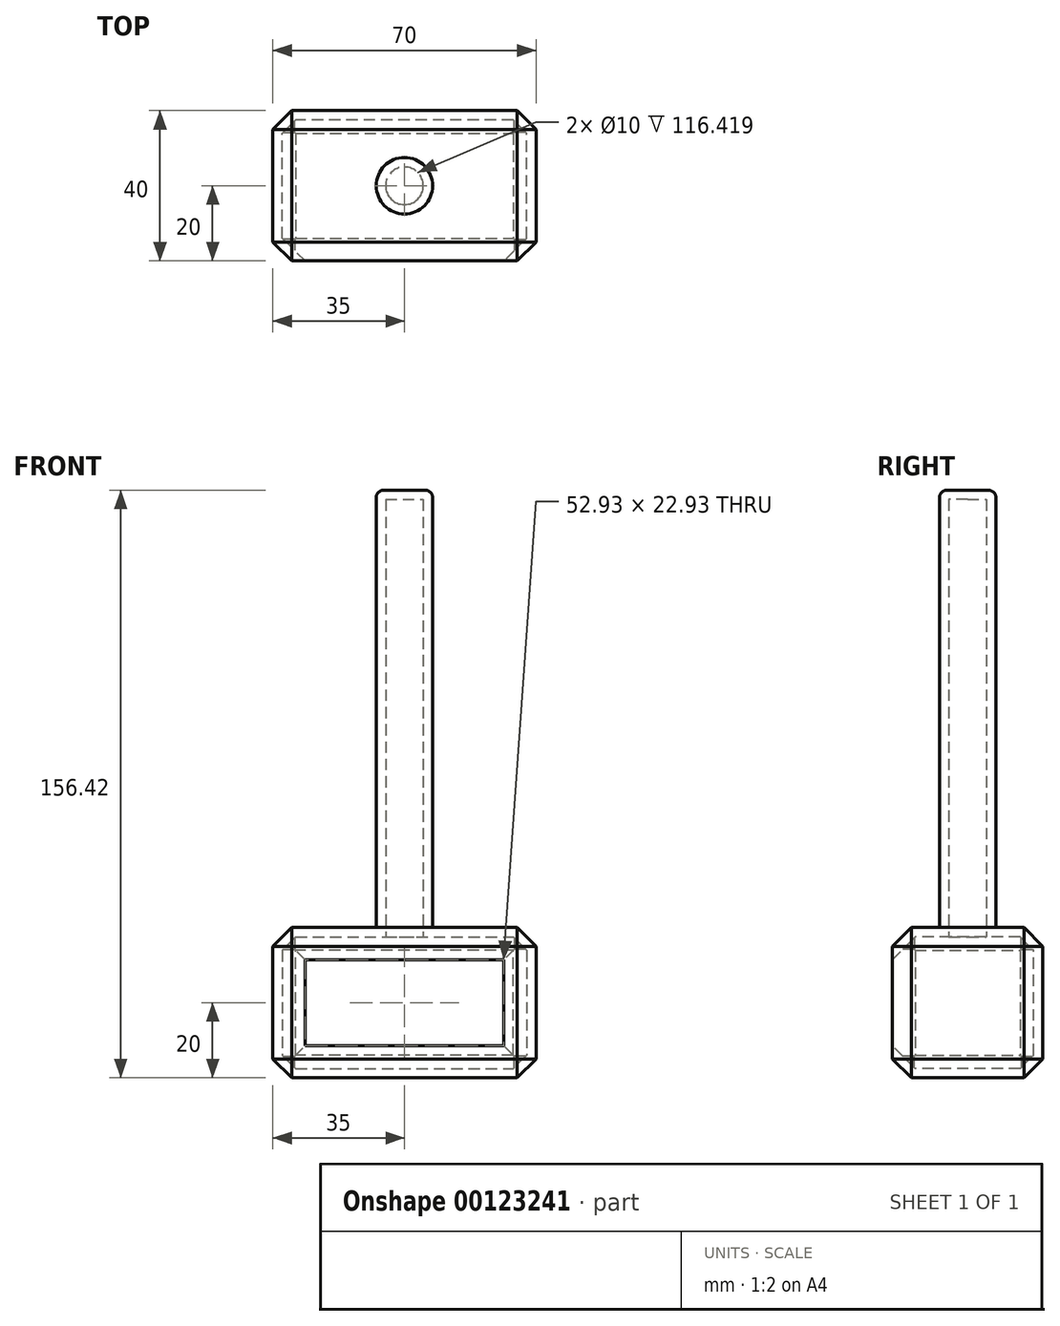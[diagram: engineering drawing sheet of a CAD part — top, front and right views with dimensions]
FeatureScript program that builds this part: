
annotation { "Feature Type Name" : "Feature", "Feature Type Description" : "" }
export const myFeature = defineFeature(function(context is Context, id is Id, definition is map)
    precondition{}
    {
        {
            var Q0;
            Q0=qCreatedBy(makeId("Front.planeOp"),FACE);
            var sketch = newSketch(context, id + "F0", { "sketchPlane" : qUnion([Q0])});
            skLineSegment(sketch, "E0", {"start": v(0, 0) * mm, "end": v(-35, 0) * mm});
            skLineSegment(sketch, "E1", {"start": v(-35, 0) * mm, "end": v(-35, 40) * mm});
            skLineSegment(sketch, "E2", {"start": v(-35, 40) * mm, "end": v(0, 40) * mm});
            skLineSegment(sketch, "E3.MirrorCS", {"start": v(35, 40) * mm, "end": v(0, 40) * mm});
            skLineSegment(sketch, "E4.MirrorCS", {"start": v(35, 0) * mm, "end": v(35, 40) * mm});
            skLineSegment(sketch, "E5.MirrorCS", {"start": v(0, 0) * mm, "end": v(35, 0) * mm});
            skSolve(sketch);
        }
        {
            var Q0;
            Q0=makeQuery(id+"F0.imprint","IMPRINT",FACE,{"disambiguationData":[TD([[makeQuery(id+"F0.imprint","IMPRINT",EDGE,{"derivedFrom":sQuery(id+"F0.wireOp",EDGE,"E0")}),-1.0]])]});
            extrude(context, id + "F1", {"entities" : qUnion([Q0]), "depth" : 40 * mm});
        }
        {
            var Q0;
            Q0=makeQuery(id+"F1.opExtrude","SWEPT_FACE",FACE,{"disambiguationData":[OSD([sQuery(id+"F0.wireOp",EDGE,"E2"),sQuery(id+"F0.wireOp",EDGE,"E3.MirrorCS")])]});
            var sketch = newSketch(context, id + "F2", { "sketchPlane" : qUnion([Q0])});
            skLineSegment(sketch, "E6", {"start": v(0, 0) * mm, "end": v(0, -20) * mm});
            skCircle(sketch, "E7", {"center": v(0, -20) * mm, "radius": 7.5 * mm});
            skSolve(sketch);
        }
        {
            var Q0;
            Q0=makeQuery(id+"F2.imprint","IMPRINT",FACE,{"disambiguationData":[TD([[makeQuery(id+"F2.imprint","IMPRINT",EDGE,{"derivedFrom":sQuery(id+"F2.wireOp",EDGE,"E7")}),1.0]])]});
            var Q1;
            Q1=sQuery(id+"F2.wireOp",EDGE,"E7");
            extrude(context, id + "F3", {"entities" : qUnion([Q0]), "operationType" : NewBodyOperationType.ADD, "surfaceEntities" : qUnion([Q1]), "depth" : 116.42 * mm});
        }
        {
            var Q0;
            Q0=makeQuery(id+"F1.opExtrude","CAP_EDGE",EDGE,{"disambiguationData":[OSD([sQuery(id+"F0.wireOp",EDGE,"E2"),sQuery(id+"F0.wireOp",EDGE,"E3.MirrorCS")])],"isStart":false});
            var Q1;
            Q1=makeQuery(id+"F1.opExtrude","SWEPT_EDGE",EDGE,{"disambiguationData":[OSD([sQuery(id+"F0.wireOp",EDGE,"E1"),sQuery(id+"F0.wireOp",EDGE,"E2")])]});
            var Q2;
            Q2=makeQuery(id+"F1.opExtrude","CAP_EDGE",EDGE,{"disambiguationData":[OSD([sQuery(id+"F0.wireOp",EDGE,"E2"),sQuery(id+"F0.wireOp",EDGE,"E3.MirrorCS")])],"isStart":true});
            var Q3;
            Q3=makeQuery(id+"F1.opExtrude","SWEPT_EDGE",EDGE,{"disambiguationData":[OSD([sQuery(id+"F0.wireOp",EDGE,"E3.MirrorCS"),sQuery(id+"F0.wireOp",EDGE,"E4.MirrorCS")])]});
            var Q4;
            Q4=makeQuery(id+"F1.opExtrude","CAP_EDGE",EDGE,{"disambiguationData":[OSD([sQuery(id+"F0.wireOp",EDGE,"E4.MirrorCS")])],"isStart":false});
            var Q5;
            Q5=makeQuery(id+"F1.opExtrude","CAP_EDGE",EDGE,{"disambiguationData":[OSD([sQuery(id+"F0.wireOp",EDGE,"E1")])],"isStart":false});
            var Q6;
            Q6=makeQuery(id+"F1.opExtrude","SWEPT_FACE",FACE,{"disambiguationData":[OSD([sQuery(id+"F0.wireOp",EDGE,"E4.MirrorCS")])]});
            var Q7;
            Q7=makeQuery(id+"F1.opExtrude","CAP_EDGE",EDGE,{"disambiguationData":[OSD([sQuery(id+"F0.wireOp",EDGE,"E0"),sQuery(id+"F0.wireOp",EDGE,"E5.MirrorCS")])],"isStart":true});
            var Q8;
            Q8=makeQuery(id+"F1.opExtrude","CAP_EDGE",EDGE,{"disambiguationData":[OSD([sQuery(id+"F0.wireOp",EDGE,"E1")])],"isStart":true});
            var Q9;
            Q9=makeQuery(id+"F1.opExtrude","SWEPT_EDGE",EDGE,{"disambiguationData":[OSD([sQuery(id+"F0.wireOp",EDGE,"E0"),sQuery(id+"F0.wireOp",EDGE,"E1")])]});
            var Q10;
            Q10=makeQuery(id+"F1.opExtrude","CAP_EDGE",EDGE,{"disambiguationData":[OSD([sQuery(id+"F0.wireOp",EDGE,"E0"),sQuery(id+"F0.wireOp",EDGE,"E5.MirrorCS")])],"isStart":false});
            chamfer(context, id + "F4", {"entities" : qUnion([Q0, Q1, Q2, Q3, Q4, Q5, Q6, Q7, Q8, Q9, Q10]), "width" : 5 * mm, "tangentPropagation" : true});
        }
        {
            var Q0;
            Q0=makeQuery(id+"F1.opExtrude","CAP_FACE",FACE,{"disambiguationData":[OSD([sQuery(id+"F0.wireOp",EDGE,"E0"),sQuery(id+"F0.wireOp",EDGE,"E1"),sQuery(id+"F0.wireOp",EDGE,"E2"),sQuery(id+"F0.wireOp",EDGE,"E3.MirrorCS"),sQuery(id+"F0.wireOp",EDGE,"E4.MirrorCS"),sQuery(id+"F0.wireOp",EDGE,"E5.MirrorCS")])],"isStart":false});
            shell(context, id + "F5", {"entities" : qUnion([Q0]), "thickness" : 2.5 * mm});
        }
        {
            var Q0;
            Q0=makeQuery(id+"F3.opExtrude","CAP_EDGE",EDGE,{"disambiguationData":[OSD([sQuery(id+"F2.wireOp",EDGE,"E7")])],"isStart":false});
            fillet(context, id + "F6", {"entities" : qUnion([Q0]), "radius" : 2 * mm, "tangentPropagation" : true, "allowEdgeOverflow" : false});
        }
        {
            var Q0;
            Q0=makeQuery(id+"F1.opExtrude","SWEPT_BODY",BODY,{"disambiguationData":[OSD([sQuery(id+"F0.wireOp",EDGE,"E0"),sQuery(id+"F0.wireOp",EDGE,"E1"),sQuery(id+"F0.wireOp",EDGE,"E2"),sQuery(id+"F0.wireOp",EDGE,"E3.MirrorCS"),sQuery(id+"F0.wireOp",EDGE,"E4.MirrorCS"),sQuery(id+"F0.wireOp",EDGE,"E5.MirrorCS")])]});
            transform(context, id + "F7", {"entities" : qUnion([Q0]), "transformType" : TransformType.TRANSLATION_3D, "dx" : 0 * mm, "dy" : 0 * mm, "dz" : 0 * mm, "makeCopy" : true});
        }
    });
